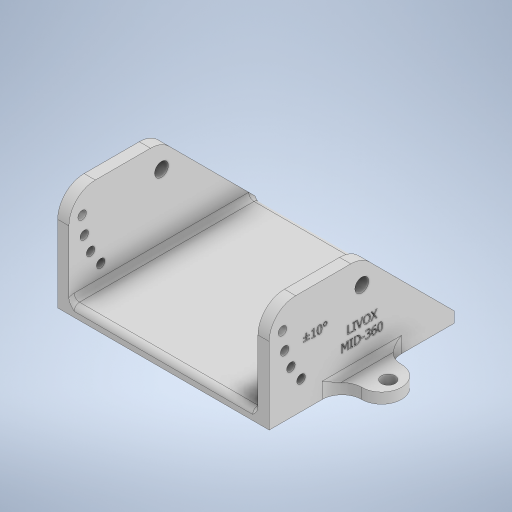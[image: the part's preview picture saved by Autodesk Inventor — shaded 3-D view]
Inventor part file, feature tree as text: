
AUTODESK INVENTOR PART (.ipt)
format: ipt  version: 2024 (Build 280153000, 153)  size: 636,416 bytes
history: native  units: mm
features: sketch x9, extrude x6, fillet x5, hole x3, other x1
ambient origin geometry x8: Origin, YZ Plane, XZ Plane, XY Plane, X Axis, Y Axis, Z Axis, Center Point
bodies: Body1 (feature_tree)
feature tree (24):
  other  "ソリッド1"
  extrude  "押し出し1"  Depth=80.0mm
  extrude  "押し出し2"  Depth=70.0mm
  hole  "穴1"  [1 undecoded]
  hole  "穴2"  [1 undecoded]
  extrude  "押し出し3"  Depth=56.0mm TaperAngle=0.0deg
  fillet  "フィレット1"  Radius=30.0mm
  fillet  "フィレット2"  Radius=30.0mm
  fillet  "フィレット3"  Radius=30.0mm
  extrude  "押し出し4"  Depth=40.0mm
  hole  "穴3"  [1 undecoded]
  fillet  "フィレット4"  [1 undecoded]
  fillet  "フィレット5"  Radius=10.0mm
  sketch  "スケッチ8"
  extrude  "押し出し5"  Depth=10.0mm
  extrude  "押し出し6"  Depth=2.0mm
  sketch  "スケッチ1"
  sketch  "スケッチ2"
  sketch  "スケッチ3"
  sketch  "スケッチ4"
  sketch  "スケッチ5"
  sketch  "スケッチ6"
  sketch  "スケッチ7"
  sketch  "スケッチ9"
note: 4 required parameter values undecoded (feature->parameter linkage not recoverable at this tier; creation-order binding heuristic only, values carry confidence <= 0.55)
